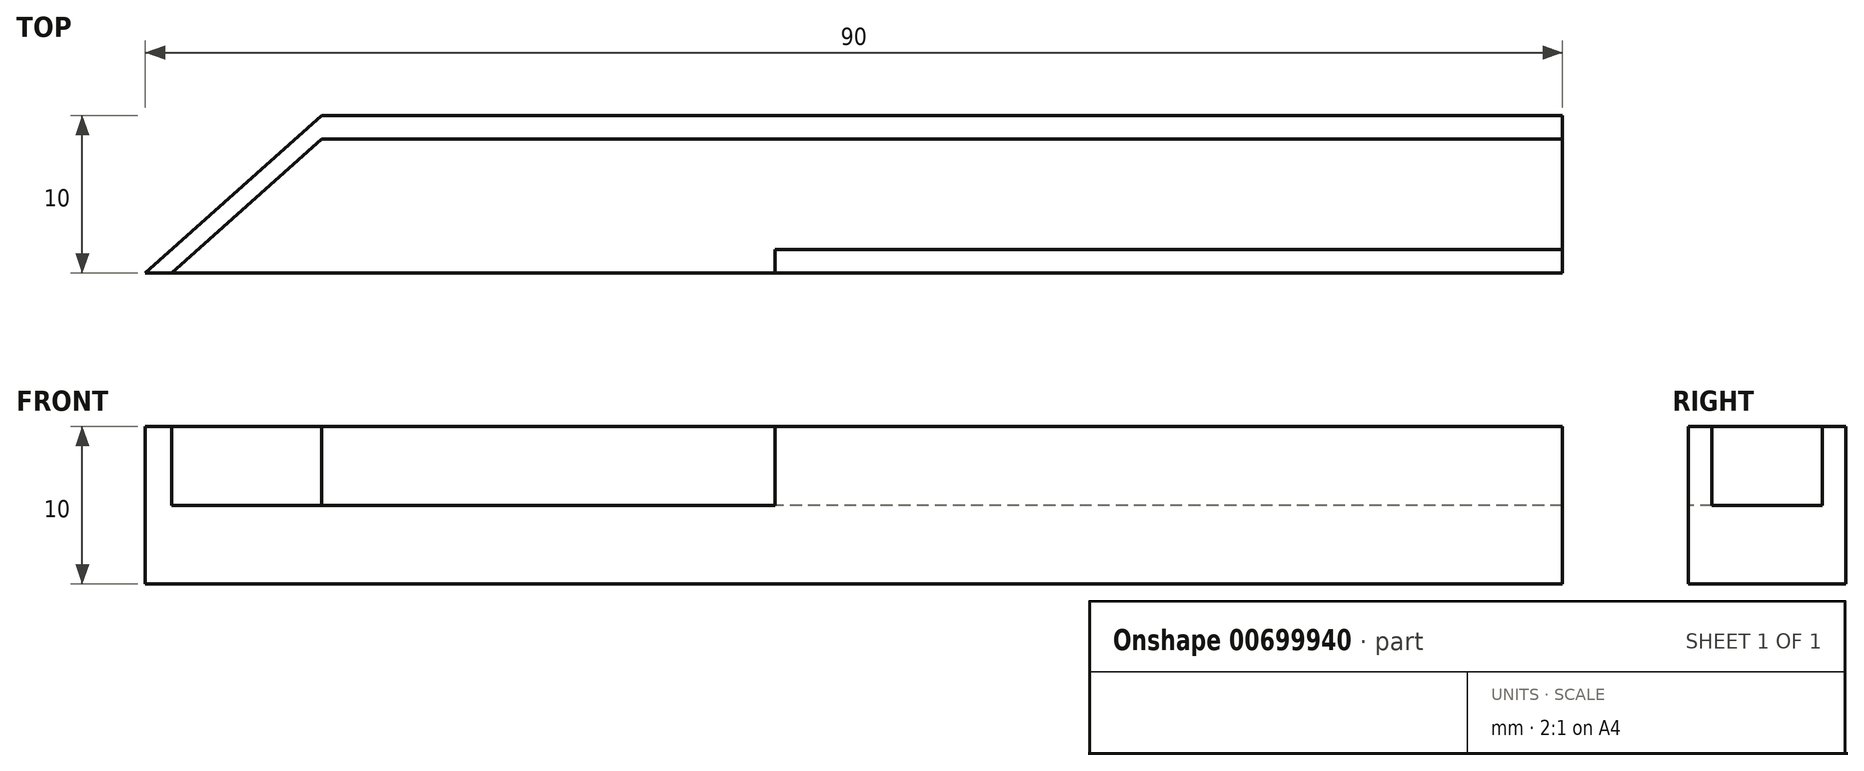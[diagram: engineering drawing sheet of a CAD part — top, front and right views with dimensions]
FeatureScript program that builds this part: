
annotation { "Feature Type Name" : "Feature", "Feature Type Description" : "" }
export const myFeature = defineFeature(function(context is Context, id is Id, definition is map)
    precondition{}
    {
        {
            var Q0;
            Q0=qCreatedBy(makeId("Top.planeOp"),FACE);
            var sketch = newSketch(context, id + "F0", { "sketchPlane" : qUnion([Q0])});
            skLineSegment(sketch, "E0.bottom", {"start": v(45, 5) * mm, "end": v(-45, 5) * mm});
            skLineSegment(sketch, "E0.top", {"start": v(45, -5) * mm, "end": v(-45, -5) * mm});
            skLineSegment(sketch, "E0.left", {"start": v(45, 5) * mm, "end": v(45, -5) * mm});
            skLineSegment(sketch, "E0.right", {"start": v(-45, 5) * mm, "end": v(-45, -5) * mm});
            skPoint(sketch, "E0.middle", {"position": v(0, 0) * mm});
            skLineSegment(sketch, "E1", {"start": v(-45, -5) * mm, "end": v(-33.82, 5) * mm});
            skSolve(sketch);
        }
        {
            var Q0;
            Q0=makeQuery(id+"F0.imprint","IMPRINT",FACE,{"disambiguationData":[TD([[makeQuery(id+"F0.imprint","IMPRINT",EDGE,{"derivedFrom":sQuery(id+"F0.wireOp",EDGE,"E0.top")}),-1.0]])]});
            extrude(context, id + "F1", {"entities" : qUnion([Q0]), "endBound" : BoundingType.SYMMETRIC, "depth" : 10 * mm, "offsetDistance" : 25 * mm});
        }
        {
            var Q0;
            Q0=makeQuery(id+"F1.opExtrude","CAP_FACE",FACE,{"disambiguationData":[OSD([sQuery(id+"F0.wireOp",EDGE,"E0.bottom"),sQuery(id+"F0.wireOp",EDGE,"E0.top"),sQuery(id+"F0.wireOp",EDGE,"E0.left"),sQuery(id+"F0.wireOp",EDGE,"E0.right")])],"isStart":false});
            var sketch = newSketch(context, id + "F2", { "sketchPlane" : qUnion([Q0])});
            skLineSegment(sketch, "E2", {"start": v(-45, -5) * mm, "end": v(-33.82, 5) * mm});
            skLineSegment(sketch, "E3", {"start": v(45, 3.5) * mm, "end": v(-33.82, 3.5) * mm});
            skLineSegment(sketch, "E4", {"start": v(-33.82, 3.5) * mm, "end": v(-33.82, 5) * mm});
            skLineSegment(sketch, "E5", {"start": v(-33.82, 3.5) * mm, "end": v(-43.32, -5) * mm});
            skLineSegment(sketch, "E6", {"start": v(45, -3.5) * mm, "end": v(-5, -3.5) * mm});
            skLineSegment(sketch, "E7", {"start": v(-5, -3.5) * mm, "end": v(-5, -5) * mm});
            skSolve(sketch);
        }
        {
            var Q0;
            {var subQ3=sQuery(id+"F2.wireOp",EDGE,"E3");Q0=makeQuery(id+"F2.imprint","IMPRINT",FACE,{"disambiguationData":[TD([[makeQuery(id+"F2.imprint","IMPRINT",EDGE,{"derivedFrom":subQ3}),1.0]])]});}
            extrude(context, id + "F3", {"entities" : qUnion([Q0]), "operationType" : NewBodyOperationType.REMOVE, "oppositeDirection" : true, "depth" : 5 * mm, "offsetDistance" : 25 * mm});
        }
    });
